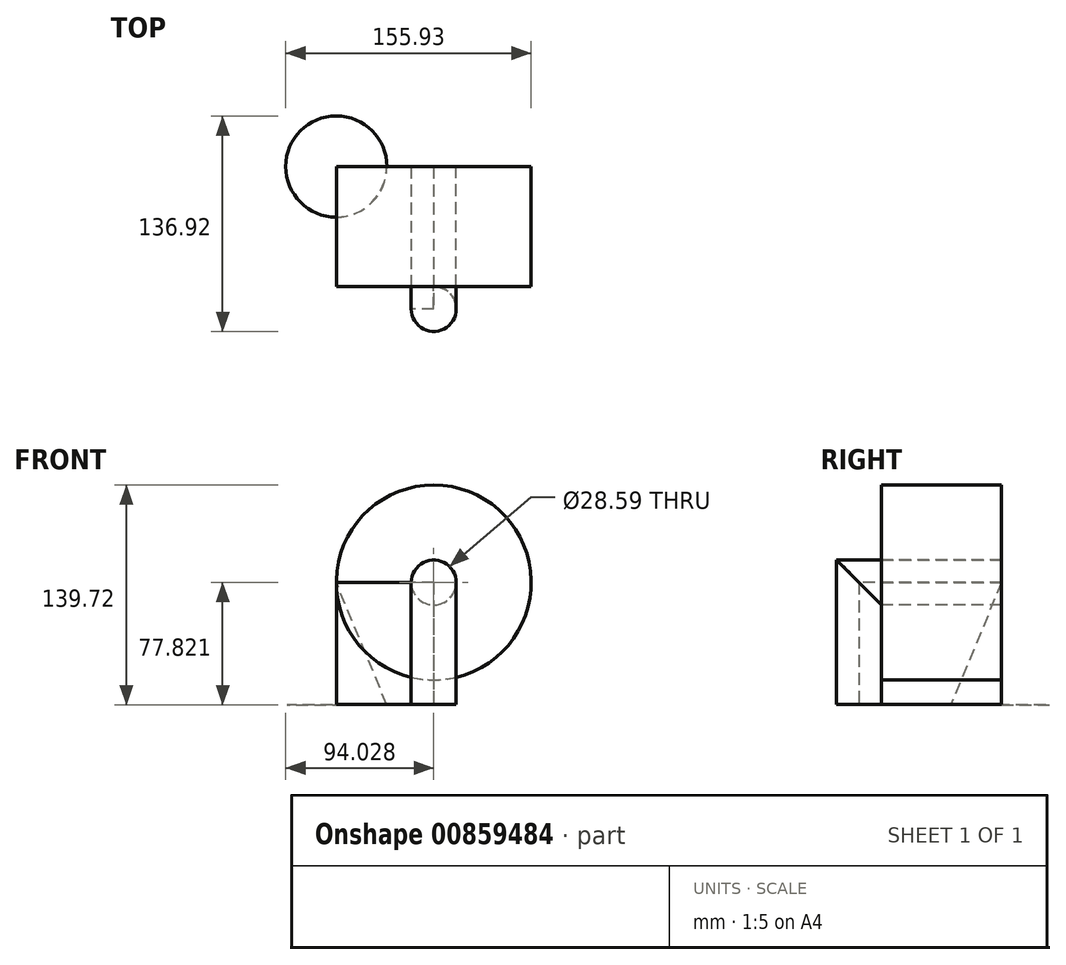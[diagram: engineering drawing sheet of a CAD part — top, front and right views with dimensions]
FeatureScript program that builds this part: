
annotation { "Feature Type Name" : "Feature", "Feature Type Description" : "" }
export const myFeature = defineFeature(function(context is Context, id is Id, definition is map)
    precondition{}
    {
        {
            var Q0;
            Q0=qCreatedBy(makeId("Front.planeOp"),FACE);
            var sketch = newSketch(context, id + "F0", { "sketchPlane" : qUnion([Q0])});
            skLineSegment(sketch, "E0", {"start": v(-32.23, 39.2) * mm, "end": v(-32.23, -38.63) * mm});
            skLineSegment(sketch, "E1", {"start": v(-32.23, -38.63) * mm, "end": v(-64.36, -38.63) * mm});
            skLineSegment(sketch, "E2", {"start": v(-64.36, -38.63) * mm, "end": v(-32.23, 39.2) * mm});
            skLineSegment(sketch, "E3.bottom", {"start": v(-32.23, 39.2) * mm, "end": v(29.67, 39.2) * mm});
            skLineSegment(sketch, "E3.top", {"start": v(-32.23, -38.4) * mm, "end": v(29.67, -38.4) * mm});
            skLineSegment(sketch, "E3.left", {"start": v(-32.23, 39.2) * mm, "end": v(-32.23, -38.4) * mm});
            skLineSegment(sketch, "E3.right", {"start": v(29.67, 39.2) * mm, "end": v(29.67, -38.4) * mm});
            skCircle(sketch, "E4", {"center": v(29.67, 39.2) * mm, "radius": 14.3 * mm});
            skSolve(sketch);
        }
        {
            var Q0;
            {var subQ1=sQuery(id+"F0.wireOp",EDGE,"E3.top");Q0=makeQuery(id+"F0.imprint","IMPRINT",FACE,{"disambiguationData":[TD([[makeQuery(id+"F0.imprint","IMPRINT",EDGE,{"derivedFrom":subQ1}),1.0]])]});}
            extrude(context, id + "F1", {"entities" : qUnion([Q0]), "depth" : 76.2 * mm, "offsetDistance" : 25.4 * mm});
        }
        {
            var Q0;
            Q0=makeQuery(id+"F0.imprint","IMPRINT",FACE,{"disambiguationData":[TD([[makeQuery(id+"F0.imprint","IMPRINT",EDGE,{"derivedFrom":sQuery(id+"F0.wireOp",EDGE,"E0")}),-1.0]])]});
            var Q1;
            Q1=sQuery(id+"F0.wireOp",EDGE,"E3.left");
            revolve(context, id + "F2", {"operationType" : NewBodyOperationType.ADD, "surfaceOperationType" : NewSurfaceOperationType.NEW, "entities" : qUnion([Q0]), "axis" : qUnion([Q1]), "revolveType" : RevolveType.ONE_DIRECTION, "angle" : 360 * degree});
        }
        {
            var Q0;
            Q0=qCreatedBy(makeId("Front.planeOp"),FACE);
            cPlane(context, id + "F3", {"entities" : qUnion([Q0]), "cplaneType" : CPlaneType.OFFSET, "offset" : 127 * mm, "width" : 152.4 * mm, "height" : 152.4 * mm});
        }
        {
            var Q0;
            {var subQ0=sQuery(id+"F0.wireOp",EDGE,"E3.right");var subQ1=sQuery(id+"F0.wireOp",EDGE,"E3.bottom");var subQ2=makeQuery(id+"F0.imprint","INTERSECT",VERTEX,{"derivedFrom":[subQ1,subQ0]});Q0=makeQuery(id+"F0.imprint","IMPRINT",FACE,{"disambiguationData":[TD([[makeQuery(id+"F0.imprint","IMPRINT",EDGE,{"disambiguationData":[TD([[subQ2,1.0]])],"derivedFrom":subQ1}),1.0]])]});}
            var Q1;
            Q1=makeQuery(id+"F1.opExtrude","SWEPT_EDGE",EDGE,{"disambiguationData":[OSD([sQuery(id+"F0.wireOp",EDGE,"E3.right"),sQuery(id+"F0.wireOp",EDGE,"E4")])]});
            var Q2;
            Q2=makeQuery(id+"F1.opExtrude","CAP_EDGE",EDGE,{"disambiguationData":[OSD([sQuery(id+"F0.wireOp",EDGE,"E3.right")])],"isStart":false});
            sweep(context, id + "F4", {"profiles" : qUnion([Q0]), "path" : qUnion([Q1, Q2])});
        }
        {
            var Q0;
            Q0=makeQuery(id+"F1.opExtrude","SWEPT_FACE",FACE,{"disambiguationData":[OSD([sQuery(id+"F0.wireOp",EDGE,"E3.bottom")])]});
            var Q1;
            {var subQ0=sQuery(id+"F0.wireOp",EDGE,"E4");var subQ1=sQuery(id+"F0.wireOp",EDGE,"E3.right");Q1=makeQuery(id+"F4.opSweep","SWEPT_FACE",FACE,{"disambiguationData":[OSD([subQ1,subQ0]),TDD([makeQuery(id+"F0.imprint","IMPRINT",EDGE,{"disambiguationData":[TD([[makeQuery(id+"F0.imprint","INTERSECT",VERTEX,{"derivedFrom":[sQuery(id+"F0.wireOp",EDGE,"E3.bottom"),subQ0]}),1.0]])],"derivedFrom":subQ0}),makeQuery(id+"F1.opExtrude","SWEPT_EDGE",EDGE,{"disambiguationData":[OSD([subQ1,subQ0])]})])]});}
            revolve(context, id + "F5", {"surfaceOperationType" : NewSurfaceOperationType.NEW, "entities" : qUnion([Q0]), "axis" : qUnion([Q1]), "revolveType" : RevolveType.FULL});
        }
    });
